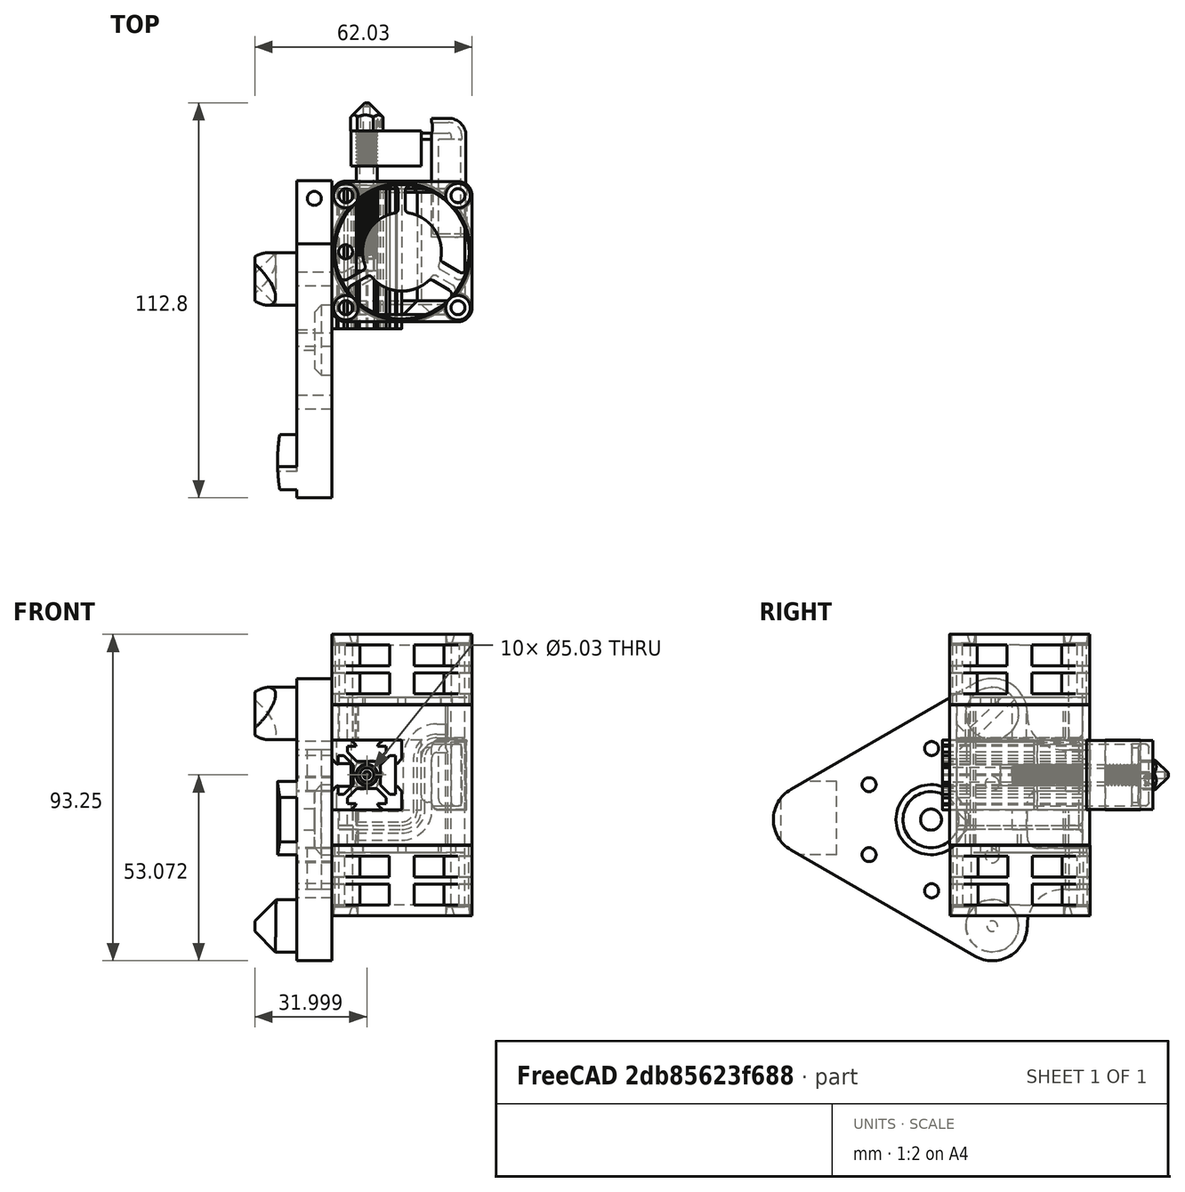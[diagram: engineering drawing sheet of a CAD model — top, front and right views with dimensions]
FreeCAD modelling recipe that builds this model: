
FCSTD DOCUMENT  (FreeCAD 0.20R29177 (Git))
Label: AT_932b_hotend_withfan
License: All rights reserved
LicenseURL: http://en.wikipedia.org/wiki/All_rights_reserved
objects: App::FeaturePython×8, Part::FeaturePython×5, PartDesign::ShapeBinder×2, Sketcher::SketchObject×1, PartDesign::Body×1
note: 9 computed .brp shape members not serialized (recipe doc carries the construction recipe); baked Part::Feature solids carry a one-line shape summary decoded from their .brp

FEATURE [Part::FeaturePython] b_AP_012a_toolHolder_GA3Dtech_001_  label="AP_012a_toolHolder_GA3Dtech_001"  # a2plus imported part (geometry in sourceFile) (typed FeaturePython)
  a2p_Version = V0.1
  fixedPosition = true
  objectType = a2pPart
  sourceFile = ./AP_012a_toolHolder_GA3Dtech.FCStd
  subassemblyImport = false
  timeLastImport = 1656487314
  updateColors = true
FEATURE [PartDesign::ShapeBinder] ShapeBinder
  Placement = pos=(-4.94089,57.1337,6.03789) rot=(0,-1,0;1.5708rad)
  TraceSupport = false
FEATURE [PartDesign::ShapeBinder] ShapeBinder001
  Support = -> [b_AP_012a_toolHolder_GA3Dtech_001_]
  TraceSupport = false
FEATURE [Sketcher::SketchObject] Sketch
  FullyConstrained = false
  MapMode = 5
  Placement = pos=(0,70.725,0) rot=(0,0.707107,0.707107;3.14159rad)
  Support = -> [ShapeBinder001]
  sketch-geometry (12):
    g0: LineSegment StartX=4.79604 StartY=5.93311 StartZ=0 EndX=92.6904 EndY=5.93311 EndZ=0
    g1-g6: Circle x6 (B-spline internal-alignment scaffolding for g7; pole/knot coordinates omitted)
    g7: BSplineCurve PolesCount=6 KnotsCount=4 Degree=3 IsPeriodic=0
    g8-g11: GeomPoint x4 (B-spline internal-alignment scaffolding for g7; pole/knot coordinates omitted)
  constraints (6):
    c: Horizontal(g0)
    c: Weight(g1) = 1
    c: Coincident(g7,g0)
    c: Equal(g1, g2-g6) x5
    c: InternalAlignment(g1-g6 -> g7) x6
    c: InternalAlignment(g8-g11 -> g7) x4
FEATURE [PartDesign::Body] Body
  Group = -> [ShapeBinder,ShapeBinder001,Sketch]
  Origin = -> Origin
FEATURE [Part::FeaturePython] b_AT_achat_fan40x40x20_001_  label="AT_achat_fan40x40x20_001"  # a2plus imported part (geometry in sourceFile) (typed FeaturePython)
  Placement = pos=(29.2359,50.666,-21.3775) rot=(0,0,1;0rad)
  a2p_Version = V0.1
  fixedPosition = false
  objectType = a2pPart
  sourceFile = ./AT_achat_fan40x40x20.FCStd
  subassemblyImport = false
  timeLastImport = 1657441506
  updateColors = true
FEATURE [Part::FeaturePython] b_AT_801a_extruder_design_001_  label="AT_801a_extruder_design_001"  # a2plus imported part (geometry in sourceFile) (typed FeaturePython)
  Placement = pos=(19.2591,25.5301,18.8125) rot=(1,0,0;4.71239rad)
  a2p_Version = V0.1
  fixedPosition = false
  objectType = a2pPart
  sourceFile = ./AT_801a_extruder_design.FCStd
  subassemblyImport = false
  timeLastImport = 1658742708
  updateColors = true
FEATURE [App::FeaturePython] planeCoincident_001  label="planeCoincident_001__AP_012a_toolHolder_GA3Dtech_001"  # a2plus constraint (typed FeaturePython)
  Object1 = b_AT_801a_extruder_design_001_
  Object2 = b_AP_012a_toolHolder_GA3Dtech_001_
  ParentTreeObject = -> b_AT_801a_extruder_design_001_
  SubElement1 = Face46
  SubElement2 = Face23
  Suppressed = false
  Type = plane
  directionConstraint = 1
  offset = 0
FEATURE [App::FeaturePython] planeCoincident_001_mirror  label="planeCoincident_001__AT_801a_extruder_design_001"  # a2plus constraint (typed FeaturePython)
  Object1 = b_AT_801a_extruder_design_001_
  Object2 = b_AP_012a_toolHolder_GA3Dtech_001_
  ParentTreeObject = -> b_AP_012a_toolHolder_GA3Dtech_001_
  SubElement1 = Face46
  SubElement2 = Face23
  Suppressed = false
  Type = plane
  directionConstraint = 1
  offset = 0
FEATURE [Part::FeaturePython] b_nozzle_mk81_001_  label="nozzle_mk81_001"  # a2plus imported part (geometry in sourceFile) (typed FeaturePython)
  Placement = pos=(19.2591,80.0301,18.8125) rot=(0.619406,-0.555129,-0.555129;4.25073rad)
  a2p_Version = V0.1
  fixedPosition = false
  objectType = a2pPart
  sourceFile = ./nozzle_mk8.step
  subassemblyImport = false
  timeLastImport = 1658742426
  updateColors = true
FEATURE [App::FeaturePython] axisCoincident_001  label="axisCoincident_001__AT_801a_extruder_design_001"  # a2plus constraint (typed FeaturePython)
  Object1 = b_nozzle_mk81_001_
  Object2 = b_AT_801a_extruder_design_001_
  ParentTreeObject = -> b_nozzle_mk81_001_
  SubElement1 = Face50
  SubElement2 = Face210
  Suppressed = false
  Type = axial
  directionConstraint = 1
  lockRotation = false
FEATURE [App::FeaturePython] axisCoincident_001_mirror  label="axisCoincident_001__nozzle_mk81_001"  # a2plus constraint (typed FeaturePython)
  Object1 = b_nozzle_mk81_001_
  Object2 = b_AT_801a_extruder_design_001_
  ParentTreeObject = -> b_AT_801a_extruder_design_001_
  SubElement1 = Face50
  SubElement2 = Face210
  Suppressed = false
  Type = axial
  directionConstraint = 1
  lockRotation = false
FEATURE [App::FeaturePython] planeCoincident_002  label="planeCoincident_002__AT_801a_extruder_design_001"  # a2plus constraint (typed FeaturePython)
  Object1 = b_nozzle_mk81_001_
  Object2 = b_AT_801a_extruder_design_001_
  ParentTreeObject = -> b_nozzle_mk81_001_
  SubElement1 = Face65
  SubElement2 = Face162
  Suppressed = false
  Type = plane
  directionConstraint = 1
  offset = 0
FEATURE [App::FeaturePython] planeCoincident_002_mirror  label="planeCoincident_002__nozzle_mk81_001"  # a2plus constraint (typed FeaturePython)
  Object1 = b_nozzle_mk81_001_
  Object2 = b_AT_801a_extruder_design_001_
  ParentTreeObject = -> b_AT_801a_extruder_design_001_
  SubElement1 = Face65
  SubElement2 = Face162
  Suppressed = false
  Type = plane
  directionConstraint = 1
  offset = 0
FEATURE [App::FeaturePython] axisCoincident_002  # a2plus constraint (typed FeaturePython)
  Object1 = b_AT_achat_fan40x40x20_001_
  Object2 = b_AT_801a_extruder_design_001_
  ParentTreeObject = -> b_AT_achat_fan40x40x20_001_
  SubElement1 = Face62
  SubElement2 = Face363
  Suppressed = false
  Type = axial
FEATURE [App::FeaturePython] axisCoincident_003  # a2plus constraint (typed FeaturePython)
  Object1 = b_AT_achat_fan40x40x20_001_
  Object2 = b_AT_801a_extruder_design_001_
  ParentTreeObject = -> b_AT_achat_fan40x40x20_001_
  SubElement1 = Face62
  SubElement2 = Face363
  Suppressed = false
  Type = axial
FEATURE [Part::FeaturePython] b_AT_achat_fan40x40x20_001_001  label="AT_achat_fan40x40x20_002"  # a2plus imported part (geometry in sourceFile) (typed FeaturePython)
  Placement = pos=(29.2928,50.4978,58.9944) rot=(0,1,0;3.14159rad)
  a2p_Version = V0.1
  fixedPosition = false
  objectType = a2pPart
  sourceFile = ./AT_achat_fan40x40x20.FCStd
  subassemblyImport = false
  timeLastImport = 1657441506
  updateColors = true
